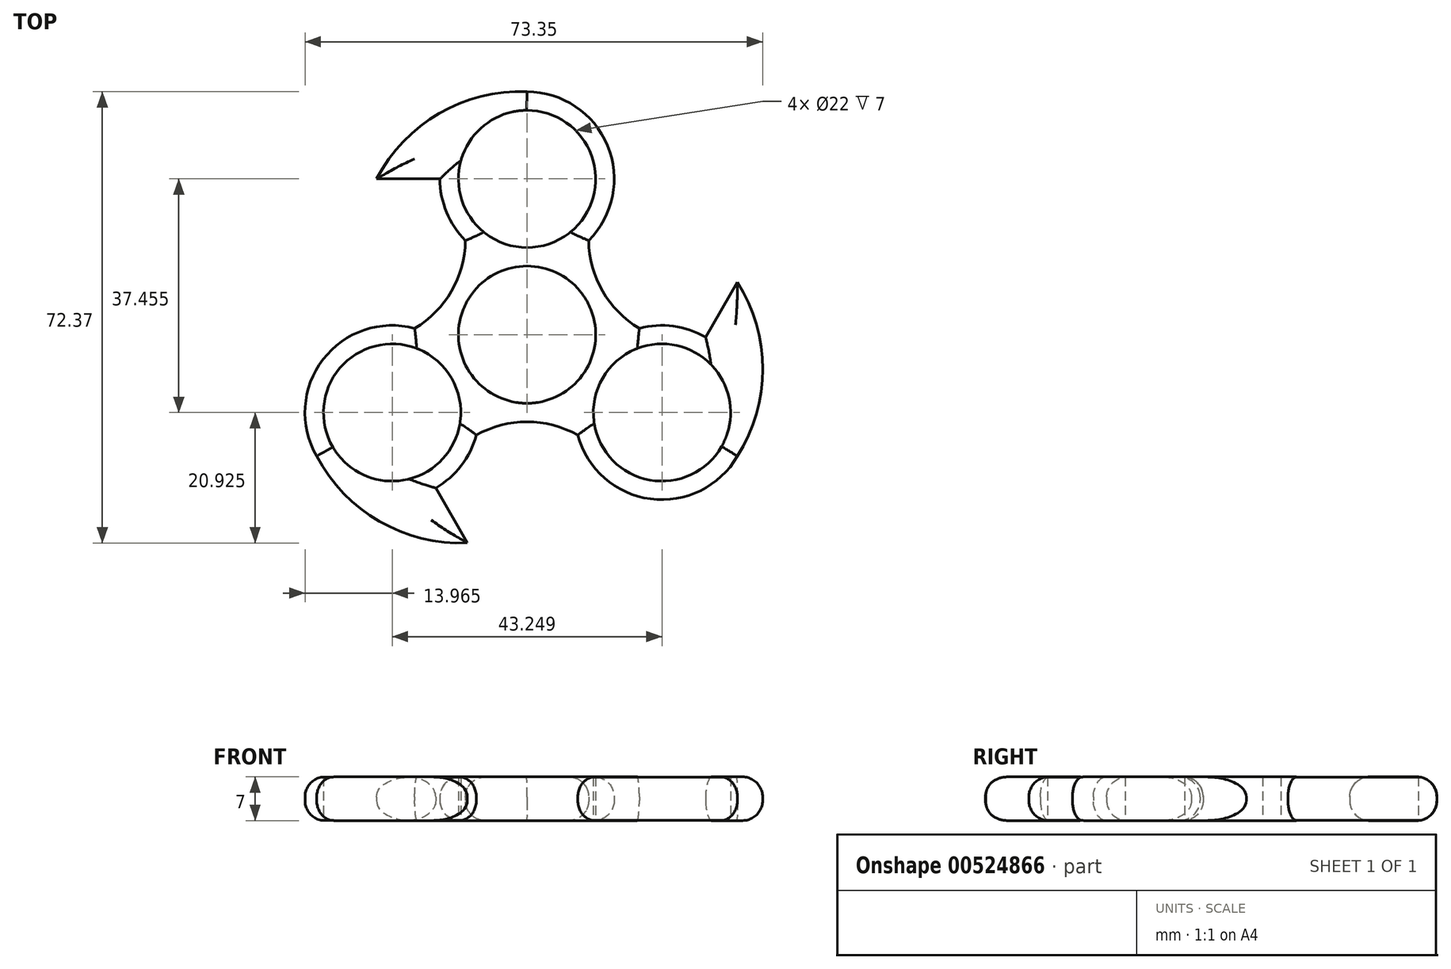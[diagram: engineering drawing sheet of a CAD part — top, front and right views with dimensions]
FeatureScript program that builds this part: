
annotation { "Feature Type Name" : "Feature", "Feature Type Description" : "" }
export const myFeature = defineFeature(function(context is Context, id is Id, definition is map)
    precondition{}
    {
        {
            var Q0;
            Q0=qCreatedBy(makeId("Top.planeOp"),FACE);
            var sketch = newSketch(context, id + "F0", { "sketchPlane" : qUnion([Q0])});
            skCircle(sketch, "E0", {"center": v(0, 0) * mm, "radius": 11 * mm});
            skCircle(sketch, "E1", {"center": v(0, 24.97) * mm, "radius": 11 * mm});
            skCircle(sketch, "E2", {"center": v(21.62, -12.48) * mm, "radius": 11 * mm});
            skCircle(sketch, "E3", {"center": v(-21.62, -12.48) * mm, "radius": 11 * mm});
            skPoint(sketch, "E4.endSnap0", {"position": v(0, -12.48) * mm});
            skArc(sketch, "E5", {"start": v(-18, 1) * mm, "mid": v(-32.7, -3.98) * mm, "end": v(-33.72, -19.47) * mm});
            skArc(sketch, "E6", {"start": v(28.6, -0.39) * mm, "mid": v(23.45, 1.37) * mm, "end": v(18, 1) * mm});
            skArc(sketch, "E7", {"start": v(9.88, 15.1) * mm, "mid": v(12.9, 30.32) * mm, "end": v(0, 38.94) * mm});
            skArc(sketch, "E8", {"start": v(9.88, 15.1) * mm, "mid": v(12.1, 6.99) * mm, "end": v(18, 1) * mm});
            skArc(sketch, "E9", {"start": v(-18, 1) * mm, "mid": v(-12.1, 6.99) * mm, "end": v(-9.88, 15.1) * mm});
            skArc(sketch, "E10", {"start": v(8.13, -16.1) * mm, "mid": v(0, -13.97) * mm, "end": v(-8.13, -16.1) * mm});
            skLineSegment(sketch, "E11", {"start": v(-13.97, 24.97) * mm, "end": v(-24.13, 24.97) * mm});
            skPoint(sketch, "E11.endSnap0", {"position": v(-12.49, 24.97) * mm});
            skLineSegment(sketch, "E12", {"start": v(-14.64, -24.58) * mm, "end": v(-9.56, -33.38) * mm});
            skLineSegment(sketch, "E13", {"start": v(28.6, -0.39) * mm, "end": v(33.69, 8.41) * mm});
            skArc(sketch, "E14", {"start": v(0, 38.94) * mm, "mid": v(-14.1, 35.46) * mm, "end": v(-24.13, 24.97) * mm});
            skArc(sketch, "E15", {"start": v(-33.72, -19.47) * mm, "mid": v(-23.66, -29.94) * mm, "end": v(-9.56, -33.38) * mm});
            skArc(sketch, "E16", {"start": v(33.72, -19.47) * mm, "mid": v(37.76, -5.52) * mm, "end": v(33.69, 8.41) * mm});
            skArc(sketch, "E17.trimOffspring", {"start": v(-14.64, -24.58) * mm, "mid": v(-10.54, -20.99) * mm, "end": v(-8.13, -16.1) * mm});
            skArc(sketch, "E18.trimOffspring", {"start": v(8.13, -16.1) * mm, "mid": v(19.8, -26.34) * mm, "end": v(33.72, -19.47) * mm});
            skArc(sketch, "E19.trimOffspring", {"start": v(-13.97, 24.97) * mm, "mid": v(-12.9, 19.62) * mm, "end": v(-9.88, 15.1) * mm});
            skSolve(sketch);
        }
        {
            var Q0;
            Q0=makeQuery(id+"F0.imprint","IMPRINT",FACE,{"disambiguationData":[TD([[makeQuery(id+"F0.imprint","IMPRINT",EDGE,{"derivedFrom":sQuery(id+"F0.wireOp",EDGE,"E0")}),-1.0]])]});
            extrude(context, id + "F1", {"entities" : qUnion([Q0]), "depth" : 7 * mm, "offsetDistance" : 25.4 * mm});
        }
        {
            var Q0;
            Q0=makeQuery(id+"F1.opExtrude","CAP_EDGE",EDGE,{"disambiguationData":[OSD([sQuery(id+"F0.wireOp",EDGE,"E5")])],"isStart":false});
            var Q1;
            Q1=makeQuery(id+"F1.opExtrude","CAP_EDGE",EDGE,{"disambiguationData":[OSD([sQuery(id+"F0.wireOp",EDGE,"E15")])],"isStart":false});
            var Q2;
            Q2=makeQuery(id+"F1.opExtrude","CAP_EDGE",EDGE,{"disambiguationData":[OSD([sQuery(id+"F0.wireOp",EDGE,"E9")])],"isStart":false});
            var Q3;
            Q3=makeQuery(id+"F1.opExtrude","CAP_EDGE",EDGE,{"disambiguationData":[OSD([sQuery(id+"F0.wireOp",EDGE,"E5")])],"isStart":true});
            var Q4;
            Q4=makeQuery(id+"F1.opExtrude","CAP_EDGE",EDGE,{"disambiguationData":[OSD([sQuery(id+"F0.wireOp",EDGE,"E15")])],"isStart":true});
            var Q5;
            Q5=makeQuery(id+"F1.opExtrude","CAP_EDGE",EDGE,{"disambiguationData":[OSD([sQuery(id+"F0.wireOp",EDGE,"E9")])],"isStart":true});
            var Q6;
            Q6=makeQuery(id+"F1.opExtrude","CAP_EDGE",EDGE,{"disambiguationData":[OSD([sQuery(id+"F0.wireOp",EDGE,"E10")])],"isStart":false});
            var Q7;
            Q7=makeQuery(id+"F1.opExtrude","CAP_EDGE",EDGE,{"disambiguationData":[OSD([sQuery(id+"F0.wireOp",EDGE,"E10")])],"isStart":true});
            var Q8;
            Q8=makeQuery(id+"F1.opExtrude","CAP_EDGE",EDGE,{"disambiguationData":[OSD([sQuery(id+"F0.wireOp",EDGE,"E18.trimOffspring")])],"isStart":false});
            var Q9;
            Q9=makeQuery(id+"F1.opExtrude","CAP_EDGE",EDGE,{"disambiguationData":[OSD([sQuery(id+"F0.wireOp",EDGE,"E18.trimOffspring")])],"isStart":true});
            var Q10;
            Q10=makeQuery(id+"F1.opExtrude","CAP_EDGE",EDGE,{"disambiguationData":[OSD([sQuery(id+"F0.wireOp",EDGE,"E16")])],"isStart":false});
            var Q11;
            Q11=makeQuery(id+"F1.opExtrude","CAP_EDGE",EDGE,{"disambiguationData":[OSD([sQuery(id+"F0.wireOp",EDGE,"E16")])],"isStart":true});
            var Q12;
            Q12=makeQuery(id+"F1.opExtrude","CAP_EDGE",EDGE,{"disambiguationData":[OSD([sQuery(id+"F0.wireOp",EDGE,"E8")])],"isStart":false});
            var Q13;
            Q13=makeQuery(id+"F1.opExtrude","CAP_EDGE",EDGE,{"disambiguationData":[OSD([sQuery(id+"F0.wireOp",EDGE,"E8")])],"isStart":true});
            var Q14;
            Q14=makeQuery(id+"F1.opExtrude","CAP_EDGE",EDGE,{"disambiguationData":[OSD([sQuery(id+"F0.wireOp",EDGE,"E14")])],"isStart":false});
            var Q15;
            Q15=makeQuery(id+"F1.opExtrude","CAP_EDGE",EDGE,{"disambiguationData":[OSD([sQuery(id+"F0.wireOp",EDGE,"E7")])],"isStart":false});
            var Q16;
            Q16=makeQuery(id+"F1.opExtrude","CAP_EDGE",EDGE,{"disambiguationData":[OSD([sQuery(id+"F0.wireOp",EDGE,"E7")])],"isStart":true});
            var Q17;
            Q17=makeQuery(id+"F1.opExtrude","CAP_EDGE",EDGE,{"disambiguationData":[OSD([sQuery(id+"F0.wireOp",EDGE,"E14")])],"isStart":true});
            var Q18;
            Q18=makeQuery(id+"F1.opExtrude","CAP_EDGE",EDGE,{"disambiguationData":[OSD([sQuery(id+"F0.wireOp",EDGE,"E11")])],"isStart":false});
            var Q19;
            Q19=makeQuery(id+"F1.opExtrude","CAP_EDGE",EDGE,{"disambiguationData":[OSD([sQuery(id+"F0.wireOp",EDGE,"E11")])],"isStart":true});
            var Q20;
            Q20=makeQuery(id+"F1.opExtrude","CAP_EDGE",EDGE,{"disambiguationData":[OSD([sQuery(id+"F0.wireOp",EDGE,"E19.trimOffspring")])],"isStart":false});
            var Q21;
            Q21=makeQuery(id+"F1.opExtrude","CAP_EDGE",EDGE,{"disambiguationData":[OSD([sQuery(id+"F0.wireOp",EDGE,"E19.trimOffspring")])],"isStart":true});
            var Q22;
            Q22=makeQuery(id+"F1.opExtrude","CAP_EDGE",EDGE,{"disambiguationData":[OSD([sQuery(id+"F0.wireOp",EDGE,"E17.trimOffspring")])],"isStart":false});
            var Q23;
            Q23=makeQuery(id+"F1.opExtrude","CAP_EDGE",EDGE,{"disambiguationData":[OSD([sQuery(id+"F0.wireOp",EDGE,"E12")])],"isStart":false});
            var Q24;
            Q24=makeQuery(id+"F1.opExtrude","CAP_EDGE",EDGE,{"disambiguationData":[OSD([sQuery(id+"F0.wireOp",EDGE,"E12")])],"isStart":true});
            var Q25;
            Q25=makeQuery(id+"F1.opExtrude","CAP_EDGE",EDGE,{"disambiguationData":[OSD([sQuery(id+"F0.wireOp",EDGE,"E17.trimOffspring")])],"isStart":true});
            var Q26;
            Q26=makeQuery(id+"F1.opExtrude","CAP_EDGE",EDGE,{"disambiguationData":[OSD([sQuery(id+"F0.wireOp",EDGE,"E13")])],"isStart":false});
            var Q27;
            Q27=makeQuery(id+"F1.opExtrude","CAP_EDGE",EDGE,{"disambiguationData":[OSD([sQuery(id+"F0.wireOp",EDGE,"E13")])],"isStart":true});
            var Q28;
            Q28=makeQuery(id+"F1.opExtrude","CAP_EDGE",EDGE,{"disambiguationData":[OSD([sQuery(id+"F0.wireOp",EDGE,"E6")])],"isStart":false});
            var Q29;
            Q29=makeQuery(id+"F1.opExtrude","CAP_EDGE",EDGE,{"disambiguationData":[OSD([sQuery(id+"F0.wireOp",EDGE,"E6")])],"isStart":true});
            fillet(context, id + "F2", {"entities" : qUnion([Q0, Q1, Q2, Q3, Q4, Q5, Q6, Q7, Q8, Q9, Q10, Q11, Q12, Q13, Q14, Q15, Q16, Q17, Q18, Q19, Q20, Q21, Q22, Q23, Q24, Q25, Q26, Q27, Q28, Q29]), "radius" : 3.2 * mm, "tangentPropagation" : true, "allowEdgeOverflow" : false});
        }
    });
